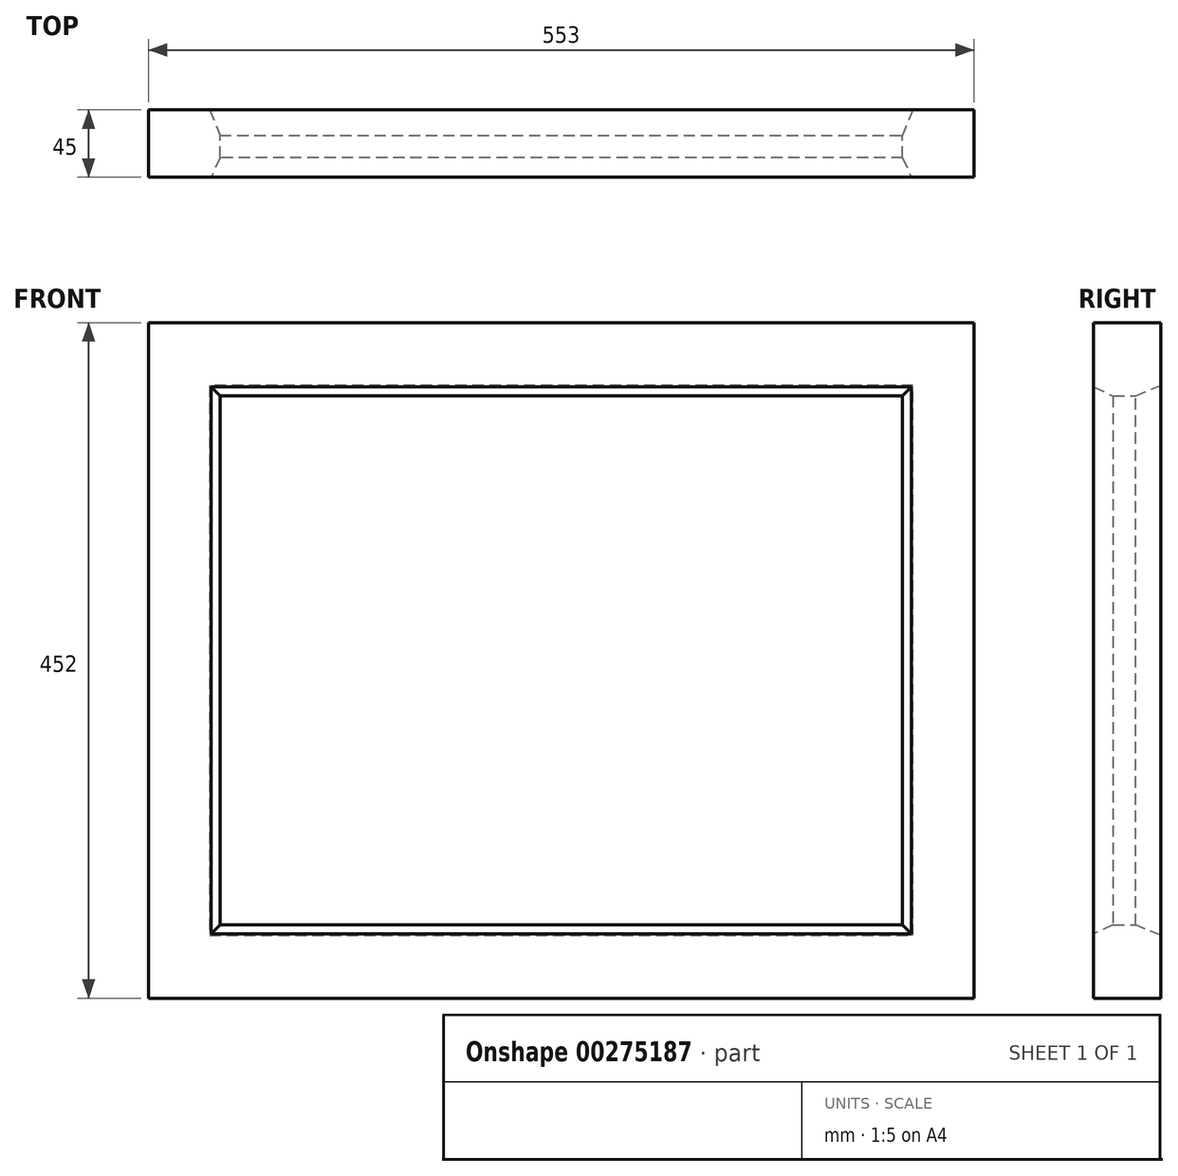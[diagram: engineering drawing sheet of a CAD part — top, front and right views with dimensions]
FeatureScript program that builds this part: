
annotation { "Feature Type Name" : "Feature", "Feature Type Description" : "" }
export const myFeature = defineFeature(function(context is Context, id is Id, definition is map)
    precondition{}
    {
        {
            var Q0;
            Q0=qCreatedBy(makeId("Front.planeOp"),FACE);
            var sketch = newSketch(context, id + "F0", { "sketchPlane" : qUnion([Q0])});
            skLineSegment(sketch, "E0.bottom", {"start": v(-276.5, 226) * mm, "end": v(276.5, 226) * mm});
            skLineSegment(sketch, "E0.top", {"start": v(-276.5, -226) * mm, "end": v(276.5, -226) * mm});
            skLineSegment(sketch, "E0.left", {"start": v(-276.5, 226) * mm, "end": v(-276.5, -226) * mm});
            skLineSegment(sketch, "E0.right", {"start": v(276.5, 226) * mm, "end": v(276.5, -226) * mm});
            skPoint(sketch, "E0.middle", {"position": v(0, 0) * mm});
            skLineSegment(sketch, "E1.bottom", {"start": v(-228.5, 177) * mm, "end": v(228.5, 177) * mm});
            skLineSegment(sketch, "E1.top", {"start": v(-228.5, -177) * mm, "end": v(228.5, -177) * mm});
            skLineSegment(sketch, "E1.left", {"start": v(-228.5, 177) * mm, "end": v(-228.5, -177) * mm});
            skLineSegment(sketch, "E1.right", {"start": v(228.5, 177) * mm, "end": v(228.5, -177) * mm});
            skSolve(sketch);
        }
        {
            var Q0;
            Q0=qSketchRegion(id+"F0",true);
            extrude(context, id + "F1", {"entities" : qUnion([Q0]), "endBound" : BoundingType.SYMMETRIC, "depth" : 45 * mm});
        }
        {
            var Q0;
            Q0=makeQuery(id+"F1.opExtrude","CAP_EDGE",EDGE,{"disambiguationData":[OSD([sQuery(id+"F0.wireOp",EDGE,"E1.top")])],"isStart":false});
            var Q1;
            Q1=makeQuery(id+"F1.opExtrude","CAP_EDGE",EDGE,{"disambiguationData":[OSD([sQuery(id+"F0.wireOp",EDGE,"E1.left")])],"isStart":false});
            var Q2;
            Q2=makeQuery(id+"F1.opExtrude","CAP_EDGE",EDGE,{"disambiguationData":[OSD([sQuery(id+"F0.wireOp",EDGE,"E1.right")])],"isStart":false});
            var Q3;
            Q3=makeQuery(id+"F1.opExtrude","CAP_EDGE",EDGE,{"disambiguationData":[OSD([sQuery(id+"F0.wireOp",EDGE,"E1.bottom")])],"isStart":false});
            chamfer(context, id + "F2", {"entities" : qUnion([Q0, Q1, Q2, Q3]), "chamferType" : ChamferType.TWO_OFFSETS, "width1" : 6 * mm, "oppositeDirection" : true, "width2" : 13 * mm, "tangentPropagation" : true});
        }
        {
            var Q0;
            Q0=makeQuery(id+"F1.opExtrude","CAP_EDGE",EDGE,{"disambiguationData":[OSD([sQuery(id+"F0.wireOp",EDGE,"E1.top")])],"isStart":true});
            var Q1;
            Q1=makeQuery(id+"F1.opExtrude","CAP_EDGE",EDGE,{"disambiguationData":[OSD([sQuery(id+"F0.wireOp",EDGE,"E1.left")])],"isStart":true});
            var Q2;
            Q2=makeQuery(id+"F1.opExtrude","CAP_EDGE",EDGE,{"disambiguationData":[OSD([sQuery(id+"F0.wireOp",EDGE,"E1.bottom")])],"isStart":true});
            var Q3;
            Q3=makeQuery(id+"F1.opExtrude","CAP_EDGE",EDGE,{"disambiguationData":[OSD([sQuery(id+"F0.wireOp",EDGE,"E1.right")])],"isStart":true});
            chamfer(context, id + "F3", {"entities" : qUnion([Q0, Q1, Q2, Q3]), "chamferType" : ChamferType.TWO_OFFSETS, "width1" : 17 * mm, "oppositeDirection" : true, "width2" : 7 * mm, "tangentPropagation" : true});
        }
    });
